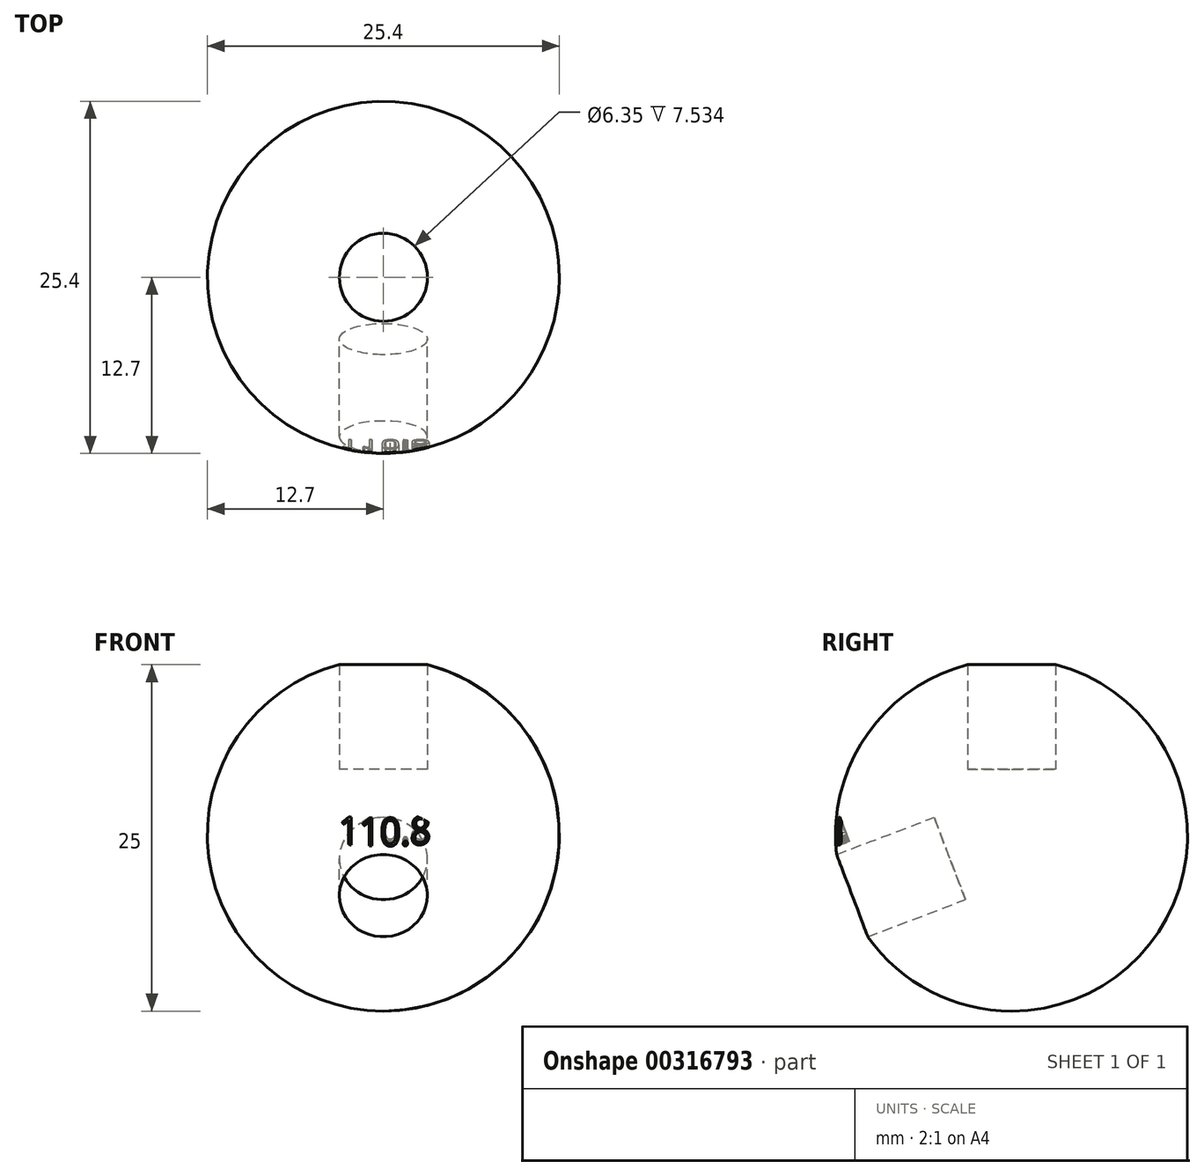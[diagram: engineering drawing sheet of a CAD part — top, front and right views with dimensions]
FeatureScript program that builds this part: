
annotation { "Feature Type Name" : "Feature", "Feature Type Description" : "" }
export const myFeature = defineFeature(function(context is Context, id is Id, definition is map)
    precondition{}
    {
        {
            var Q0;
            Q0=qCreatedBy(makeId("Front.planeOp"),FACE);
            var sketch = newSketch(context, id + "F0", { "sketchPlane" : qUnion([Q0])});
            skArc(sketch, "E0", {"start": v(0, 12.7) * mm, "mid": v(-12.7, 0) * mm, "end": v(0, -12.7) * mm});
            skLineSegment(sketch, "E1", {"start": v(0, 12.7) * mm, "end": v(0, -12.7) * mm});
            skSolve(sketch);
        }
        {
            var Q0;
            Q0 = qSketchRegion(id + "F0", true);
            var Q1;
            Q1=sQuery(id+"F0.wireOp",EDGE,"E1");
            revolve(context, id + "F1", {"entities" : qUnion([Q0]), "axis" : qUnion([Q1]), "revolveType" : RevolveType.FULL});
        }
        {
            var Q0;
            Q0=qCreatedBy(makeId("Top.planeOp"),FACE);
            cPlane(context, id + "F2", {"entities" : qUnion([Q0]), "cplaneType" : CPlaneType.OFFSET, "offset" : 4.76 * mm, "width" : 152.4 * mm, "height" : 152.4 * mm});
        }
        {
            var Q0;
            Q0=qCreatedBy(id+"F2.planeOp",FACE);
            var sketch = newSketch(context, id + "F3", { "sketchPlane" : qUnion([Q0])});
            skCircle(sketch, "E2", {"center": v(0, 0) * mm, "radius": 3.18 * mm});
            skSolve(sketch);
        }
        {
            var Q0;
            Q0 = qSketchRegion(id + "F3", true);
            extrude(context, id + "F4", {"entities" : qUnion([Q0]), "depth" : 25.4 * mm});
        }
        {
            var Q0;
            Q0=qCreatedBy(makeId("Front.planeOp"),FACE);
            var sketch = newSketch(context, id + "F5", { "sketchPlane" : qUnion([Q0])});
            skLineSegment(sketch, "E3", {"start": v(0, 0) * mm, "end": v(53.28, 0) * mm, "construction": true});
            skLineSegment(sketch, "E4", {"start": v(53.28, 0) * mm, "end": v(-32.26, 0) * mm, "construction": true});
            skLineSegment(sketch, "E5", {"start": v(0, 0) * mm, "end": v(0, 47.93) * mm, "construction": true});
            skLineSegment(sketch, "E6", {"start": v(0, 47.93) * mm, "end": v(0, -37.6) * mm, "construction": true});
            skSolve(sketch);
        }
        {
            var Q0;
            Q0=makeQuery(id+"F4.opExtrude","SWEPT_BODY",BODY,{"disambiguationData":[OSD([sQuery(id+"F3.wireOp",EDGE,"E2")])]});
            var Q1;
            Q1=sQuery(id+"F5.wireOp",EDGE,"E3");
            transform(context, id + "F6", {"entities" : qUnion([Q0]), "transformType" : TransformType.ROTATION, "transformAxis" : qUnion([Q1]), "angle" : 110.8 * degree, "makeCopy" : true});
        }
        {
            var Q0;
            Q0=makeQuery(id+"F6.opPattern","COPY",FACE,{"derivedFrom":makeQuery(id+"F4.opExtrude","CAP_FACE",FACE,{"disambiguationData":[OSD([sQuery(id+"F3.wireOp",EDGE,"E2")])],"isStart":false}),"instanceName":"1"});
            cPlane(context, id + "F7", {"entities" : qUnion([Q0]), "cplaneType" : CPlaneType.OFFSET, "offset" : 12.7 * mm, "oppositeDirection" : true, "width" : 152.4 * mm, "height" : 152.4 * mm});
        }
        {
            var Q0;
            Q0=qCreatedBy(id+"F7.planeOp",FACE);
            var sketch = newSketch(context, id + "F8", { "sketchPlane" : qUnion([Q0])});
            skText(sketch, "E7", { "text": "110.8", "fontName": "OpenSans-Regular.ttf"});
            const initialGuessF8  = {"E7": [-0.00321, 0.00377, 1, 0, 0.00187]};
            skSetInitialGuess(sketch, initialGuessF8);
            skSolve(sketch);
        }
        {
            var Q0;
            Q0 = qSketchRegion(id + "F8", true);
            extrude(context, id + "F9", {"entities" : qUnion([Q0]), "operationType" : NewBodyOperationType.REMOVE, "oppositeDirection" : true, "depth" : 6.35 * mm});
        }
        {
            var Q0;
            Q0=makeQuery(id+"F6.opPattern","COPY",BODY,{"derivedFrom":makeQuery(id+"F4.opExtrude","SWEPT_BODY",BODY,{"disambiguationData":[OSD([sQuery(id+"F3.wireOp",EDGE,"E2")])]}),"instanceName":"1"});
            var Q1;
            Q1=makeQuery(id+"F4.opExtrude","SWEPT_BODY",BODY,{"disambiguationData":[OSD([sQuery(id+"F3.wireOp",EDGE,"E2")])]});
            var Q2;
            Q2=makeQuery(id+"F1.opRevolve","SWEPT_BODY",BODY,{"disambiguationData":[OSD([sQuery(id+"F0.wireOp",EDGE,"E0"),sQuery(id+"F0.wireOp",EDGE,"E1")])]});
            booleanBodies(context, id + "F10", {"operationType" : BooleanOperationType.SUBTRACTION, "tools" : qUnion([Q0, Q1]), "targets" : qUnion([Q2])});
        }
    });
